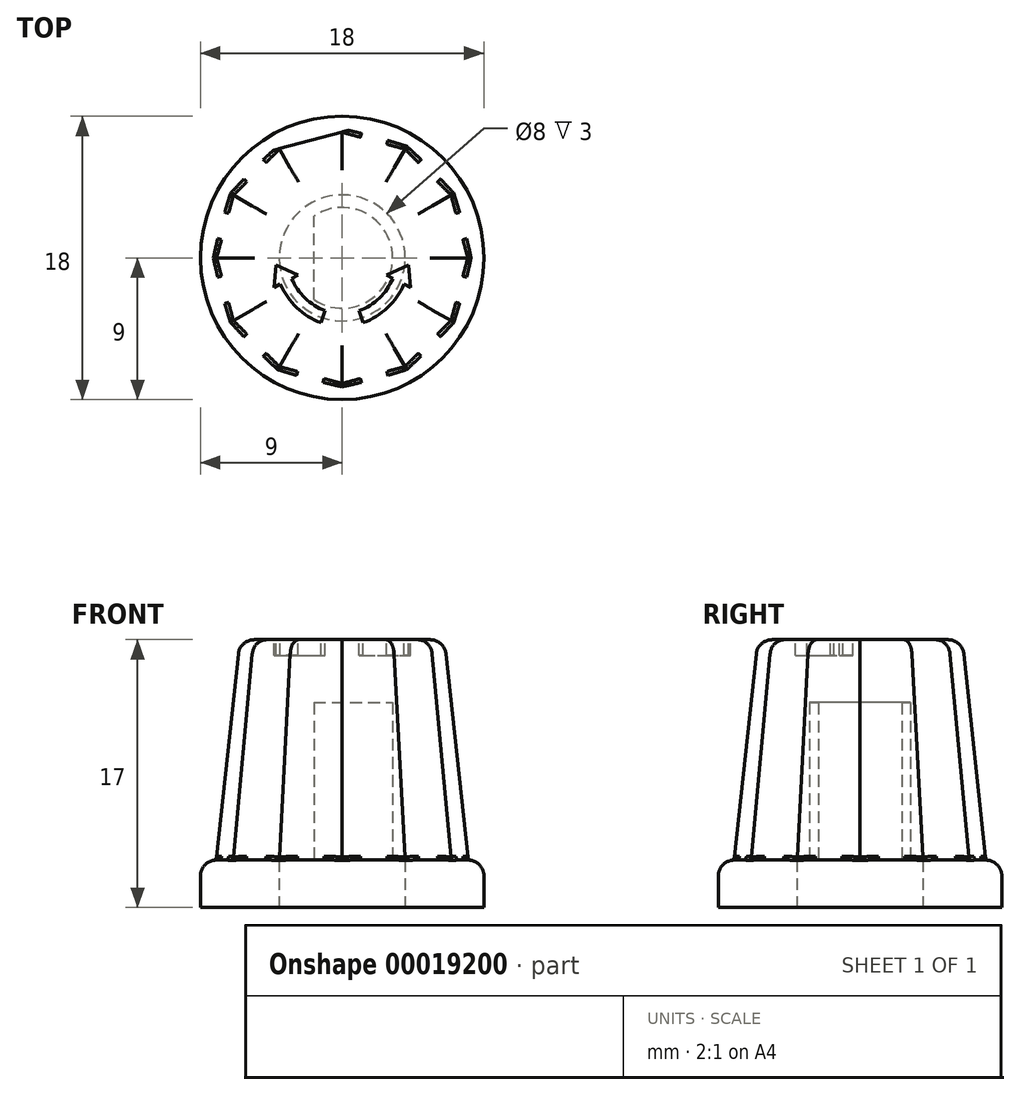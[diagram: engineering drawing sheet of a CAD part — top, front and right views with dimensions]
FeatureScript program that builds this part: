
annotation { "Feature Type Name" : "Feature", "Feature Type Description" : "" }
export const myFeature = defineFeature(function(context is Context, id is Id, definition is map)
    precondition{}
    {
        {
            var Q0;
            Q0=qCreatedBy(makeId("Top.planeOp"),FACE);
            var sketch = newSketch(context, id + "F0", { "sketchPlane" : qUnion([Q0])});
            skCircle(sketch, "E0", {"center": v(0, 0) * mm, "radius": 8 * mm});
            skSolve(sketch);
        }
        {
            var Q0;
            Q0=makeQuery(id+"F0.imprint","IMPRINT",FACE,{"disambiguationData":[TD([[makeQuery(id+"F0.imprint","IMPRINT",EDGE,{"derivedFrom":sQuery(id+"F0.wireOp",EDGE,"E0")}),1.0]])]});
            extrude(context, id + "F1", {"entities" : qUnion([Q0]), "depth" : 3 * mm});
        }
        {
            var Q0;
            Q0=makeQuery(id+"F1.opExtrude","CAP_FACE",FACE,{"disambiguationData":[OSD([sQuery(id+"F0.wireOp",EDGE,"E0")])],"isStart":false});
            var sketch = newSketch(context, id + "F2", { "sketchPlane" : qUnion([Q0])});
            skCircle(sketch, "E1.cCircle", {"center": v(0, 0) * mm, "radius": 8 * mm, "construction": true});
            skLineSegment(sketch, "E1.0", {"start": v(0, 8) * mm, "end": v(4, 6.93) * mm});
            skLineSegment(sketch, "E1.1", {"start": v(4, 6.93) * mm, "end": v(6.93, 4) * mm});
            skLineSegment(sketch, "E1.2", {"start": v(6.93, 4) * mm, "end": v(8, 0) * mm});
            skLineSegment(sketch, "E1.3", {"start": v(8, 0) * mm, "end": v(6.93, -4) * mm});
            skLineSegment(sketch, "E1.4", {"start": v(6.93, -4) * mm, "end": v(4, -6.93) * mm});
            skLineSegment(sketch, "E1.5", {"start": v(4, -6.93) * mm, "end": v(0, -8) * mm});
            skLineSegment(sketch, "E1.6", {"start": v(0, -8) * mm, "end": v(-4, -6.93) * mm});
            skLineSegment(sketch, "E1.7", {"start": v(-4, -6.93) * mm, "end": v(-6.93, -4) * mm});
            skLineSegment(sketch, "E1.8", {"start": v(-6.93, -4) * mm, "end": v(-8, 0) * mm});
            skLineSegment(sketch, "E1.9", {"start": v(-8, 0) * mm, "end": v(-6.93, 4) * mm});
            skLineSegment(sketch, "E1.10", {"start": v(-6.93, 4) * mm, "end": v(-4, 6.93) * mm});
            skLineSegment(sketch, "E1.11", {"start": v(-4, 6.93) * mm, "end": v(0, 8) * mm});
            skSolve(sketch);
        }
        {
            var Q0;
            Q0=makeQuery(id+"F2.imprint","IMPRINT",FACE,{"disambiguationData":[TD([[makeQuery(id+"F2.imprint","IMPRINT",EDGE,{"derivedFrom":sQuery(id+"F2.wireOp",EDGE,"E1.0")}),-1.0]])]});
            cPlane(context, id + "F3", {"entities" : qUnion([Q0]), "cplaneType" : CPlaneType.OFFSET, "offset" : 14 * mm, "width" : 150 * mm, "height" : 150 * mm});
        }
        {
            var Q0;
            Q0=qCreatedBy(id+"F3.planeOp",FACE);
            var sketch = newSketch(context, id + "F4", { "sketchPlane" : qUnion([Q0])});
            skCircle(sketch, "E2.cCircle", {"center": v(0, 0) * mm, "radius": 6.5 * mm, "construction": true});
            skLineSegment(sketch, "E2.0", {"start": v(0, 6.5) * mm, "end": v(3.25, 5.63) * mm});
            skLineSegment(sketch, "E2.1", {"start": v(3.25, 5.63) * mm, "end": v(5.63, 3.25) * mm});
            skLineSegment(sketch, "E2.2", {"start": v(5.63, 3.25) * mm, "end": v(6.5, 0) * mm});
            skLineSegment(sketch, "E2.3", {"start": v(6.5, 0) * mm, "end": v(5.63, -3.25) * mm});
            skLineSegment(sketch, "E2.4", {"start": v(5.63, -3.25) * mm, "end": v(3.25, -5.63) * mm});
            skLineSegment(sketch, "E2.5", {"start": v(3.25, -5.63) * mm, "end": v(0, -6.5) * mm});
            skLineSegment(sketch, "E2.6", {"start": v(0, -6.5) * mm, "end": v(-3.25, -5.63) * mm});
            skLineSegment(sketch, "E2.7", {"start": v(-3.25, -5.63) * mm, "end": v(-5.63, -3.25) * mm});
            skLineSegment(sketch, "E2.8", {"start": v(-5.63, -3.25) * mm, "end": v(-6.5, 0) * mm});
            skLineSegment(sketch, "E2.9", {"start": v(-6.5, 0) * mm, "end": v(-5.63, 3.25) * mm});
            skLineSegment(sketch, "E2.10", {"start": v(-5.63, 3.25) * mm, "end": v(-3.25, 5.63) * mm});
            skLineSegment(sketch, "E2.11", {"start": v(-3.25, 5.63) * mm, "end": v(0, 6.5) * mm});
            skSolve(sketch);
        }
        {
            var Q1;
            Q1=makeQuery(id+"F2.imprint","IMPRINT",FACE,{"disambiguationData":[TD([[makeQuery(id+"F2.imprint","IMPRINT",EDGE,{"derivedFrom":sQuery(id+"F2.wireOp",EDGE,"E1.0")}),-1.0]])]});
            var Q2;
            Q2=makeQuery(id+"F4.imprint","IMPRINT",FACE,{"disambiguationData":[TD([[makeQuery(id+"F4.imprint","IMPRINT",EDGE,{"derivedFrom":sQuery(id+"F4.wireOp",EDGE,"E2.0")}),-1.0]])]});
            loft(context, id + "F5", {"operationType" : NewBodyOperationType.ADD, "sheetProfilesArray" : [{ "sheetProfileEntities" : qUnion([Q1]) }, { "sheetProfileEntities" : qUnion([Q2]) }]});
        }
        {
            var Q0;
            Q0=makeQuery(id+"F1.opExtrude","CAP_FACE",FACE,{"disambiguationData":[OSD([sQuery(id+"F0.wireOp",EDGE,"E0")])],"isStart":true});
            var sketch = newSketch(context, id + "F6", { "sketchPlane" : qUnion([Q0])});
            skArc(sketch, "E3", {"start": v(-1.8, -2.65) * mm, "mid": v(3.2, 0) * mm, "end": v(-1.8, 2.65) * mm});
            skLineSegment(sketch, "E4", {"start": v(-1.8, -2.65) * mm, "end": v(-1.8, 2.65) * mm});
            skSolve(sketch);
        }
        {
            var Q0;
            Q0 = qSketchRegion(id + "F6", true);
            extrude(context, id + "F7", {"entities" : qUnion([Q0]), "operationType" : NewBodyOperationType.REMOVE, "oppositeDirection" : true, "depth" : 13 * mm});
        }
        {
            var Q0;
            Q0=makeQuery(id+"F5.opLoft","MID_CAP_EDGE",EDGE,{"disambiguationData":[OSD([sQuery(id+"F4.wireOp",EDGE,"E2.4"),sQuery(id+"F4.wireOp",EDGE,"E2.5"),sQuery(id+"F4.wireOp",EDGE,"E2.6")])],"capPos":1.0});
            var Q1;
            Q1=makeQuery(id+"F5.opLoft","MID_CAP_EDGE",EDGE,{"disambiguationData":[OSD([sQuery(id+"F4.wireOp",EDGE,"E2.5"),sQuery(id+"F4.wireOp",EDGE,"E2.6"),sQuery(id+"F4.wireOp",EDGE,"E2.7")])],"capPos":1.0});
            var Q2;
            Q2=makeQuery(id+"F5.opLoft","MID_CAP_EDGE",EDGE,{"disambiguationData":[OSD([sQuery(id+"F4.wireOp",EDGE,"E2.6"),sQuery(id+"F4.wireOp",EDGE,"E2.7"),sQuery(id+"F4.wireOp",EDGE,"E2.8")])],"capPos":1.0});
            var Q3;
            Q3=makeQuery(id+"F5.opLoft","MID_CAP_EDGE",EDGE,{"disambiguationData":[OSD([sQuery(id+"F4.wireOp",EDGE,"E2.7"),sQuery(id+"F4.wireOp",EDGE,"E2.8"),sQuery(id+"F4.wireOp",EDGE,"E2.9")])],"capPos":1.0});
            var Q4;
            Q4=makeQuery(id+"F5.opLoft","MID_CAP_EDGE",EDGE,{"disambiguationData":[OSD([sQuery(id+"F4.wireOp",EDGE,"E2.8"),sQuery(id+"F4.wireOp",EDGE,"E2.9"),sQuery(id+"F4.wireOp",EDGE,"E2.10")])],"capPos":1.0});
            var Q5;
            Q5=makeQuery(id+"F5.opLoft","MID_CAP_EDGE",EDGE,{"disambiguationData":[OSD([sQuery(id+"F4.wireOp",EDGE,"E2.9"),sQuery(id+"F4.wireOp",EDGE,"E2.10"),sQuery(id+"F4.wireOp",EDGE,"E2.11")])],"capPos":1.0});
            var Q6;
            Q6=makeQuery(id+"F5.opLoft","MID_CAP_EDGE",EDGE,{"disambiguationData":[OSD([sQuery(id+"F4.wireOp",EDGE,"E2.0"),sQuery(id+"F4.wireOp",EDGE,"E2.10"),sQuery(id+"F4.wireOp",EDGE,"E2.11")])],"capPos":1.0});
            var Q7;
            Q7=makeQuery(id+"F5.opLoft","MID_CAP_EDGE",EDGE,{"disambiguationData":[OSD([sQuery(id+"F4.wireOp",EDGE,"E2.0"),sQuery(id+"F4.wireOp",EDGE,"E2.1"),sQuery(id+"F4.wireOp",EDGE,"E2.11")])],"capPos":1.0});
            var Q8;
            Q8=makeQuery(id+"F5.opLoft","MID_CAP_EDGE",EDGE,{"disambiguationData":[OSD([sQuery(id+"F4.wireOp",EDGE,"E2.0"),sQuery(id+"F4.wireOp",EDGE,"E2.1"),sQuery(id+"F4.wireOp",EDGE,"E2.2")])],"capPos":1.0});
            var Q9;
            Q9=makeQuery(id+"F5.opLoft","MID_CAP_EDGE",EDGE,{"disambiguationData":[OSD([sQuery(id+"F4.wireOp",EDGE,"E2.1"),sQuery(id+"F4.wireOp",EDGE,"E2.2"),sQuery(id+"F4.wireOp",EDGE,"E2.3")])],"capPos":1.0});
            var Q10;
            Q10=makeQuery(id+"F5.opLoft","MID_CAP_EDGE",EDGE,{"disambiguationData":[OSD([sQuery(id+"F4.wireOp",EDGE,"E2.2"),sQuery(id+"F4.wireOp",EDGE,"E2.3"),sQuery(id+"F4.wireOp",EDGE,"E2.4")])],"capPos":1.0});
            var Q11;
            Q11=makeQuery(id+"F5.opLoft","MID_CAP_EDGE",EDGE,{"disambiguationData":[OSD([sQuery(id+"F4.wireOp",EDGE,"E2.3"),sQuery(id+"F4.wireOp",EDGE,"E2.4"),sQuery(id+"F4.wireOp",EDGE,"E2.5")])],"capPos":1.0});
            fillet(context, id + "F8", {"entities" : qUnion([Q0, Q1, Q2, Q3, Q4, Q5, Q6, Q7, Q8, Q9, Q10, Q11]), "radius" : 1 * mm, "tangentPropagation" : true, "allowEdgeOverflow" : false});
        }
        {
            var Q0;
            Q0=makeQuery(id+"F1.opExtrude","CAP_FACE",FACE,{"disambiguationData":[OSD([sQuery(id+"F0.wireOp",EDGE,"E0")])],"isStart":true});
            var sketch = newSketch(context, id + "F9", { "sketchPlane" : qUnion([Q0])});
            skCircle(sketch, "E5", {"center": v(0, 0) * mm, "radius": 9 * mm});
            skCircle(sketch, "E6", {"center": v(0, 0) * mm, "radius": 8 * mm});
            skSolve(sketch);
        }
        {
            var Q0;
            Q0 = qSketchRegion(id + "F9", true);
            extrude(context, id + "F10", {"entities" : qUnion([Q0]), "operationType" : NewBodyOperationType.ADD, "oppositeDirection" : true, "depth" : 3 * mm});
        }
        {
            var Q0;
            Q0=makeQuery(id+"F10.opExtrude","CAP_EDGE",EDGE,{"disambiguationData":[OSD([sQuery(id+"F9.wireOp",EDGE,"E5")])],"isStart":false});
            fillet(context, id + "F11", {"entities" : qUnion([Q0]), "radius" : 1 * mm, "tangentPropagation" : true, "allowEdgeOverflow" : false});
        }
        {
            var Q0;
            Q0=makeQuery(id+"F5.opLoft","MID_CAP_EDGE",EDGE,{"disambiguationData":[OSD([sQuery(id+"F0.wireOp",EDGE,"E0"),sQuery(id+"F2.wireOp",EDGE,"E1.1"),sQuery(id+"F2.wireOp",EDGE,"E1.2"),sQuery(id+"F2.wireOp",EDGE,"E1.3")])],"capPos":0.0});
            var Q1;
            Q1=makeQuery(id+"F5.opLoft","MID_CAP_EDGE",EDGE,{"disambiguationData":[OSD([sQuery(id+"F0.wireOp",EDGE,"E0"),sQuery(id+"F2.wireOp",EDGE,"E1.0"),sQuery(id+"F2.wireOp",EDGE,"E1.1"),sQuery(id+"F2.wireOp",EDGE,"E1.2")])],"capPos":0.0});
            var Q2;
            Q2=makeQuery(id+"F5.opLoft","MID_CAP_EDGE",EDGE,{"disambiguationData":[OSD([sQuery(id+"F0.wireOp",EDGE,"E0"),sQuery(id+"F2.wireOp",EDGE,"E1.0"),sQuery(id+"F2.wireOp",EDGE,"E1.1"),sQuery(id+"F2.wireOp",EDGE,"E1.11")])],"capPos":0.0});
            var Q3;
            Q3=makeQuery(id+"F5.opLoft","MID_CAP_EDGE",EDGE,{"disambiguationData":[OSD([sQuery(id+"F0.wireOp",EDGE,"E0"),sQuery(id+"F2.wireOp",EDGE,"E1.0"),sQuery(id+"F2.wireOp",EDGE,"E1.10"),sQuery(id+"F2.wireOp",EDGE,"E1.11")])],"capPos":0.0});
            var Q4;
            Q4=makeQuery(id+"F5.opLoft","MID_CAP_EDGE",EDGE,{"disambiguationData":[OSD([sQuery(id+"F0.wireOp",EDGE,"E0"),sQuery(id+"F2.wireOp",EDGE,"E1.9"),sQuery(id+"F2.wireOp",EDGE,"E1.10"),sQuery(id+"F2.wireOp",EDGE,"E1.11")])],"capPos":0.0});
            var Q5;
            Q5=makeQuery(id+"F5.opLoft","MID_CAP_EDGE",EDGE,{"disambiguationData":[OSD([sQuery(id+"F0.wireOp",EDGE,"E0"),sQuery(id+"F2.wireOp",EDGE,"E1.8"),sQuery(id+"F2.wireOp",EDGE,"E1.9"),sQuery(id+"F2.wireOp",EDGE,"E1.10")])],"capPos":0.0});
            var Q6;
            Q6=makeQuery(id+"F5.opLoft","MID_CAP_EDGE",EDGE,{"disambiguationData":[OSD([sQuery(id+"F0.wireOp",EDGE,"E0"),sQuery(id+"F2.wireOp",EDGE,"E1.7"),sQuery(id+"F2.wireOp",EDGE,"E1.8"),sQuery(id+"F2.wireOp",EDGE,"E1.9")])],"capPos":0.0});
            var Q7;
            Q7=makeQuery(id+"F5.opLoft","MID_CAP_EDGE",EDGE,{"disambiguationData":[OSD([sQuery(id+"F0.wireOp",EDGE,"E0"),sQuery(id+"F2.wireOp",EDGE,"E1.6"),sQuery(id+"F2.wireOp",EDGE,"E1.7"),sQuery(id+"F2.wireOp",EDGE,"E1.8")])],"capPos":0.0});
            var Q8;
            Q8=makeQuery(id+"F5.opLoft","MID_CAP_EDGE",EDGE,{"disambiguationData":[OSD([sQuery(id+"F0.wireOp",EDGE,"E0"),sQuery(id+"F2.wireOp",EDGE,"E1.5"),sQuery(id+"F2.wireOp",EDGE,"E1.6"),sQuery(id+"F2.wireOp",EDGE,"E1.7")])],"capPos":0.0});
            var Q9;
            Q9=makeQuery(id+"F5.opLoft","MID_CAP_EDGE",EDGE,{"disambiguationData":[OSD([sQuery(id+"F0.wireOp",EDGE,"E0"),sQuery(id+"F2.wireOp",EDGE,"E1.4"),sQuery(id+"F2.wireOp",EDGE,"E1.5"),sQuery(id+"F2.wireOp",EDGE,"E1.6")])],"capPos":0.0});
            var Q10;
            Q10=makeQuery(id+"F5.opLoft","MID_CAP_EDGE",EDGE,{"disambiguationData":[OSD([sQuery(id+"F0.wireOp",EDGE,"E0"),sQuery(id+"F2.wireOp",EDGE,"E1.2"),sQuery(id+"F2.wireOp",EDGE,"E1.3"),sQuery(id+"F2.wireOp",EDGE,"E1.4")])],"capPos":0.0});
            var Q11;
            Q11=makeQuery(id+"F5.opLoft","MID_CAP_EDGE",EDGE,{"disambiguationData":[OSD([sQuery(id+"F0.wireOp",EDGE,"E0"),sQuery(id+"F2.wireOp",EDGE,"E1.3"),sQuery(id+"F2.wireOp",EDGE,"E1.4"),sQuery(id+"F2.wireOp",EDGE,"E1.5")])],"capPos":0.0});
            fillet(context, id + "F12", {"entities" : qUnion([Q0, Q1, Q2, Q3, Q4, Q5, Q6, Q7, Q8, Q9, Q10, Q11]), "radius" : .25 * mm, "tangentPropagation" : true, "allowEdgeOverflow" : false});
        }
        {
            var Q0;
            Q0=makeQuery(id+"F10.boolean.opBoolean","MERGE",FACE,{"derivedFrom":[makeQuery(id+"F1.opExtrude","CAP_FACE",FACE,{"disambiguationData":[OSD([sQuery(id+"F0.wireOp",EDGE,"E0")])],"isStart":true}),makeQuery(id+"F10.opExtrude","CAP_FACE",FACE,{"disambiguationData":[OSD([sQuery(id+"F9.wireOp",EDGE,"E5"),sQuery(id+"F9.wireOp",EDGE,"E6")])],"isStart":true})]});
            var sketch = newSketch(context, id + "F13", { "sketchPlane" : qUnion([Q0])});
            skCircle(sketch, "E7", {"center": v(0, 0) * mm, "radius": 4 * mm});
            skSolve(sketch);
        }
        {
            var Q0;
            Q0 = qSketchRegion(id + "F13", true);
            extrude(context, id + "F14", {"entities" : qUnion([Q0]), "operationType" : NewBodyOperationType.REMOVE, "oppositeDirection" : true, "depth" : 3 * mm});
        }
        {
            var Q0;
            Q0=makeQuery(id+"F5.opLoft","CAP_FACE",FACE,{"disambiguationData":[OSD([makeQuery(id+"F4.imprint","IMPRINT",FACE,{"disambiguationData":[TD([[makeQuery(id+"F4.imprint","IMPRINT",EDGE,{"derivedFrom":sQuery(id+"F4.wireOp",EDGE,"E2.0")}),-1.0]])]})])],"isStart":true});
            var sketch = newSketch(context, id + "F15", { "sketchPlane" : qUnion([Q0])});
            skArc(sketch, "E8", {"start": v(-3.22, -1.3) * mm, "mid": v(-2.36, -2.55) * mm, "end": v(-1.08, -3.36) * mm});
            skArc(sketch, "E9.0", {"start": v(-3.93, -1.66) * mm, "mid": v(-2.89, -3.16) * mm, "end": v(-1.34, -4.12) * mm});
            skLineSegment(sketch, "E10", {"start": v(-4.2, -0.44) * mm, "end": v(-4.32, -1.9) * mm});
            skLineSegment(sketch, "E11", {"start": v(-4.32, -1.9) * mm, "end": v(-3.93, -1.66) * mm});
            skLineSegment(sketch, "E12", {"start": v(-3.22, -1.3) * mm, "end": v(-3.22, -1.3) * mm});
            skLineSegment(sketch, "E13", {"start": v(-1.34, -4.12) * mm, "end": v(-1.08, -3.36) * mm});
            skLineSegment(sketch, "E14", {"start": v(-3.22, -1.3) * mm, "end": v(-2.82, -1.1) * mm});
            skLineSegment(sketch, "E15", {"start": v(-2.82, -1.1) * mm, "end": v(-4.2, -0.44) * mm});
            skLineSegment(sketch, "E16.MirrorCS", {"start": v(1.34, -4.12) * mm, "end": v(1.08, -3.36) * mm});
            skArc(sketch, "E17.MirrorCS", {"start": v(3.93, -1.66) * mm, "mid": v(2.89, -3.16) * mm, "end": v(1.34, -4.12) * mm});
            skArc(sketch, "E18.MirrorCS", {"start": v(3.22, -1.3) * mm, "mid": v(2.36, -2.55) * mm, "end": v(1.08, -3.36) * mm});
            skLineSegment(sketch, "E19.MirrorCS", {"start": v(3.22, -1.3) * mm, "end": v(2.82, -1.1) * mm});
            skLineSegment(sketch, "E20.MirrorCS", {"start": v(2.82, -1.1) * mm, "end": v(4.2, -0.44) * mm});
            skLineSegment(sketch, "E21.MirrorCS", {"start": v(4.2, -0.44) * mm, "end": v(4.32, -1.9) * mm});
            skLineSegment(sketch, "E22.MirrorCS", {"start": v(4.32, -1.9) * mm, "end": v(3.93, -1.66) * mm});
            skSolve(sketch);
        }
        {
            var Q0;
            Q0 = qSketchRegion(id + "F15", true);
            extrude(context, id + "F16", {"entities" : qUnion([Q0]), "operationType" : NewBodyOperationType.REMOVE, "oppositeDirection" : true, "depth" : 1 * mm});
        }
    });
